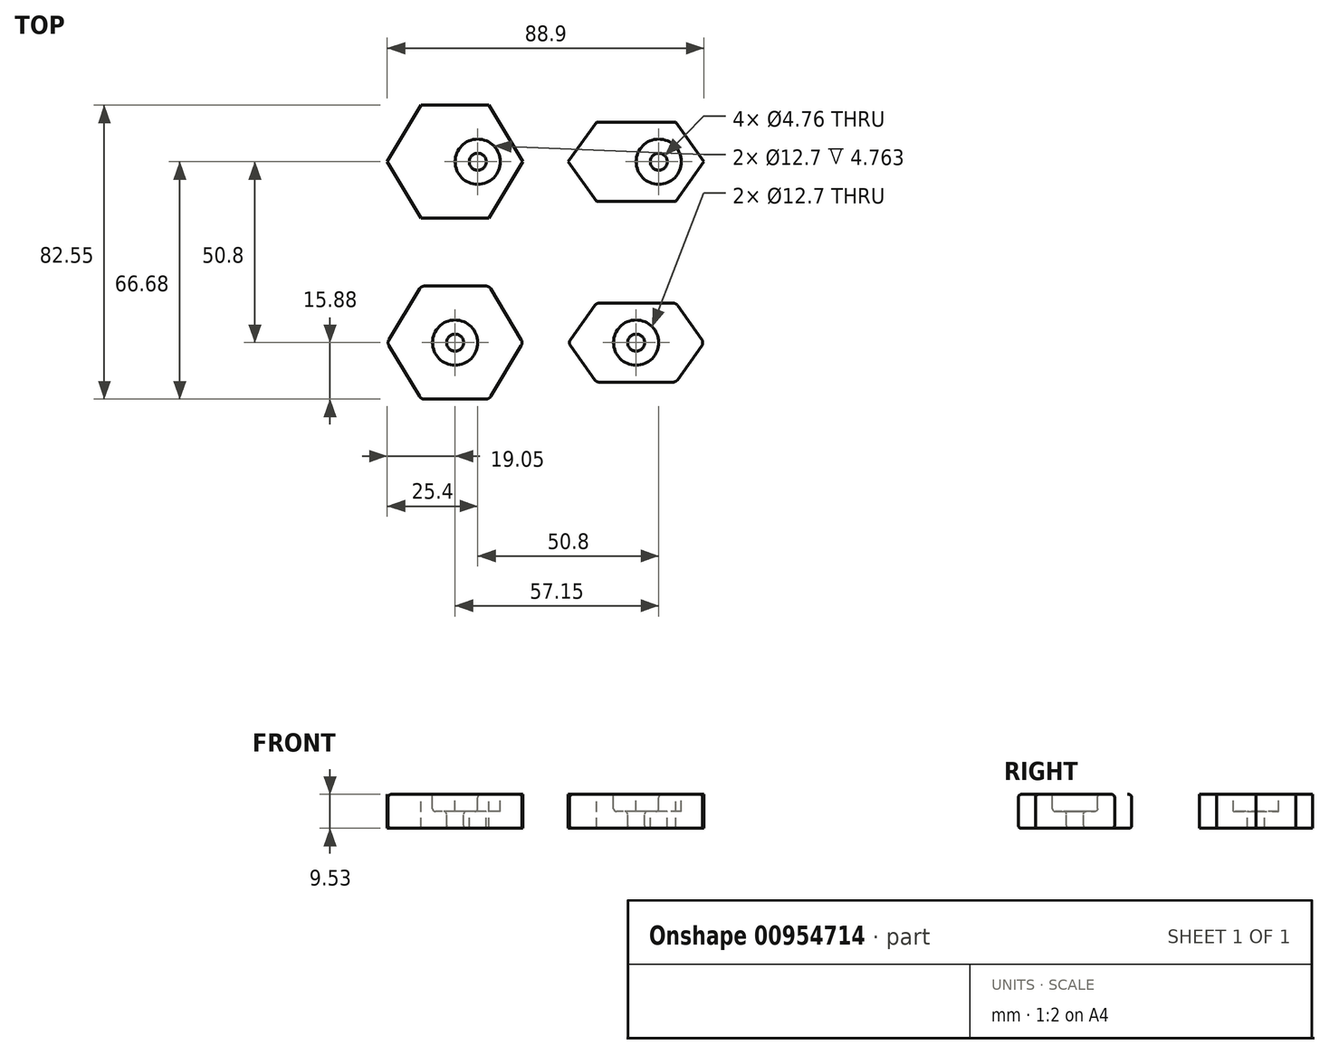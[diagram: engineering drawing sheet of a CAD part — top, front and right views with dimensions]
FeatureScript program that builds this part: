
annotation { "Feature Type Name" : "Feature", "Feature Type Description" : "" }
export const myFeature = defineFeature(function(context is Context, id is Id, definition is map)
    precondition{}
    {
        {
            var Q0;
            Q0=qCreatedBy(makeId("Top.planeOp"),FACE);
            var sketch = newSketch(context, id + "F0", { "sketchPlane" : qUnion([Q0])});
            skArc(sketch, "E0", {"start": v(61.09, 11.11) * mm, "mid": v(61.82, 10.94) * mm, "end": v(62.4, 10.44) * mm});
            skLineSegment(sketch, "E1", {"start": v(62.4, 10.44) * mm, "end": v(69.18, 0.93) * mm});
            skArc(sketch, "E2", {"start": v(69.18, 0.93) * mm, "mid": v(69.49, 0) * mm, "end": v(69.18, -0.93) * mm});
            skLineSegment(sketch, "E3", {"start": v(69.18, -0.93) * mm, "end": v(62.4, -10.44) * mm});
            skArc(sketch, "E4", {"start": v(62.4, -10.44) * mm, "mid": v(61.82, -10.94) * mm, "end": v(61.09, -11.11) * mm});
            skLineSegment(sketch, "E5", {"start": v(61.09, -11.11) * mm, "end": v(40.51, -11.11) * mm});
            skArc(sketch, "E6", {"start": v(40.51, -11.11) * mm, "mid": v(39.78, -10.94) * mm, "end": v(39.2, -10.44) * mm});
            skLineSegment(sketch, "E7", {"start": v(39.2, -10.44) * mm, "end": v(32.42, -0.93) * mm});
            skArc(sketch, "E8", {"start": v(32.42, -0.93) * mm, "mid": v(32.11, 0) * mm, "end": v(32.42, 0.93) * mm});
            skLineSegment(sketch, "E9", {"start": v(32.42, 0.93) * mm, "end": v(39.2, 10.44) * mm});
            skArc(sketch, "E10", {"start": v(39.2, 10.44) * mm, "mid": v(39.78, 10.94) * mm, "end": v(40.51, 11.11) * mm});
            skLineSegment(sketch, "E11", {"start": v(40.51, 11.11) * mm, "end": v(61.09, 11.11) * mm});
            skArc(sketch, "E12", {"start": v(-18.55, -0.83) * mm, "mid": v(-18.79, 0) * mm, "end": v(-18.55, 0.83) * mm});
            skLineSegment(sketch, "E13", {"start": v(-18.55, 0.83) * mm, "end": v(-10, 15.1) * mm});
            skArc(sketch, "E14", {"start": v(-10, 15.1) * mm, "mid": v(-9.4, 15.67) * mm, "end": v(-8.62, 15.87) * mm});
            skLineSegment(sketch, "E15", {"start": v(-8.62, 15.88) * mm, "end": v(8.62, 15.88) * mm});
            skArc(sketch, "E16", {"start": v(8.62, 15.87) * mm, "mid": v(9.4, 15.67) * mm, "end": v(10, 15.1) * mm});
            skLineSegment(sketch, "E17", {"start": v(10, 15.1) * mm, "end": v(18.55, 0.83) * mm});
            skArc(sketch, "E18", {"start": v(18.55, 0.83) * mm, "mid": v(18.79, 0) * mm, "end": v(18.55, -0.83) * mm});
            skLineSegment(sketch, "E19", {"start": v(18.55, -0.83) * mm, "end": v(10, -15.1) * mm});
            skArc(sketch, "E20", {"start": v(10, -15.1) * mm, "mid": v(9.4, -15.67) * mm, "end": v(8.62, -15.87) * mm});
            skLineSegment(sketch, "E21", {"start": v(8.62, -15.88) * mm, "end": v(-8.62, -15.88) * mm});
            skArc(sketch, "E22", {"start": v(-8.62, -15.87) * mm, "mid": v(-9.4, -15.67) * mm, "end": v(-10, -15.1) * mm});
            skLineSegment(sketch, "E23", {"start": v(-10, -15.1) * mm, "end": v(-18.55, -0.83) * mm});
            skArc(sketch, "E24", {"start": v(3.97, 50.8) * mm, "mid": v(4.67, 49.12) * mm, "end": v(6.35, 48.42) * mm});
            skArc(sketch, "E25", {"start": v(6.35, 48.42) * mm, "mid": v(8.03, 49.12) * mm, "end": v(8.73, 50.8) * mm});
            skArc(sketch, "E26", {"start": v(8.73, 50.8) * mm, "mid": v(8.03, 52.48) * mm, "end": v(6.35, 53.18) * mm});
            skArc(sketch, "E27", {"start": v(6.35, 53.18) * mm, "mid": v(4.67, 52.48) * mm, "end": v(3.97, 50.8) * mm});
            skArc(sketch, "E28", {"start": v(0, 50.8) * mm, "mid": v(1.86, 55.3) * mm, "end": v(6.35, 57.15) * mm});
            skArc(sketch, "E29", {"start": v(6.35, 57.15) * mm, "mid": v(10.84, 55.3) * mm, "end": v(12.7, 50.8) * mm});
            skArc(sketch, "E30", {"start": v(12.7, 50.8) * mm, "mid": v(10.84, 46.3) * mm, "end": v(6.35, 44.45) * mm});
            skArc(sketch, "E31", {"start": v(6.35, 44.45) * mm, "mid": v(1.86, 46.3) * mm, "end": v(0, 50.8) * mm});
            skLineSegment(sketch, "E32", {"start": v(-9.53, 34.93) * mm, "end": v(-19.05, 50.8) * mm});
            skLineSegment(sketch, "E33", {"start": v(-19.05, 50.8) * mm, "end": v(-9.52, 66.68) * mm});
            skLineSegment(sketch, "E34", {"start": v(-9.53, 66.68) * mm, "end": v(9.53, 66.68) * mm});
            skLineSegment(sketch, "E35", {"start": v(9.53, 66.68) * mm, "end": v(19.05, 50.8) * mm});
            skLineSegment(sketch, "E36", {"start": v(19.05, 50.8) * mm, "end": v(9.52, 34.92) * mm});
            skLineSegment(sketch, "E37", {"start": v(9.53, 34.93) * mm, "end": v(-9.53, 34.93) * mm});
            skLineSegment(sketch, "E38", {"start": v(39.69, 39.69) * mm, "end": v(31.75, 50.8) * mm});
            skLineSegment(sketch, "E39", {"start": v(31.75, 50.8) * mm, "end": v(39.69, 61.91) * mm});
            skLineSegment(sketch, "E40", {"start": v(39.69, 61.91) * mm, "end": v(61.91, 61.91) * mm});
            skLineSegment(sketch, "E41", {"start": v(61.91, 61.91) * mm, "end": v(69.85, 50.8) * mm});
            skLineSegment(sketch, "E42", {"start": v(69.85, 50.8) * mm, "end": v(61.91, 39.69) * mm});
            skLineSegment(sketch, "E43", {"start": v(61.91, 39.69) * mm, "end": v(39.69, 39.69) * mm});
            skArc(sketch, "E44", {"start": v(54.77, 50.8) * mm, "mid": v(55.47, 49.12) * mm, "end": v(57.15, 48.42) * mm});
            skArc(sketch, "E45", {"start": v(57.15, 48.42) * mm, "mid": v(58.83, 49.12) * mm, "end": v(59.53, 50.8) * mm});
            skArc(sketch, "E46", {"start": v(59.53, 50.8) * mm, "mid": v(58.83, 52.48) * mm, "end": v(57.15, 53.18) * mm});
            skArc(sketch, "E47", {"start": v(57.15, 53.18) * mm, "mid": v(55.47, 52.48) * mm, "end": v(54.77, 50.8) * mm});
            skArc(sketch, "E48", {"start": v(50.8, 50.8) * mm, "mid": v(52.66, 55.3) * mm, "end": v(57.15, 57.15) * mm});
            skArc(sketch, "E49", {"start": v(57.15, 57.15) * mm, "mid": v(61.64, 55.3) * mm, "end": v(63.5, 50.8) * mm});
            skArc(sketch, "E50", {"start": v(63.5, 50.8) * mm, "mid": v(61.64, 46.3) * mm, "end": v(57.15, 44.45) * mm});
            skArc(sketch, "E51", {"start": v(57.15, 44.45) * mm, "mid": v(52.66, 46.3) * mm, "end": v(50.8, 50.8) * mm});
            skArc(sketch, "E52", {"start": v(-2.38, 0) * mm, "mid": v(-1.68, -1.68) * mm, "end": v(0, -2.38) * mm});
            skArc(sketch, "E53", {"start": v(0, -2.38) * mm, "mid": v(1.68, -1.68) * mm, "end": v(2.38, 0) * mm});
            skArc(sketch, "E54", {"start": v(2.38, 0) * mm, "mid": v(1.68, 1.68) * mm, "end": v(0, 2.38) * mm});
            skArc(sketch, "E55", {"start": v(0, 2.38) * mm, "mid": v(-1.68, 1.68) * mm, "end": v(-2.38, 0) * mm});
            skArc(sketch, "E56", {"start": v(-6.35, 0) * mm, "mid": v(-4.5, 4.5) * mm, "end": v(0, 6.35) * mm});
            skArc(sketch, "E57", {"start": v(0, 6.35) * mm, "mid": v(4.5, 4.5) * mm, "end": v(6.35, 0) * mm});
            skArc(sketch, "E58", {"start": v(6.35, 0) * mm, "mid": v(4.5, -4.5) * mm, "end": v(0, -6.35) * mm});
            skArc(sketch, "E59", {"start": v(0, -6.35) * mm, "mid": v(-4.5, -4.5) * mm, "end": v(-6.35, 0) * mm});
            skArc(sketch, "E60", {"start": v(48.42, 0) * mm, "mid": v(49.12, -1.68) * mm, "end": v(50.8, -2.38) * mm});
            skArc(sketch, "E61", {"start": v(50.8, -2.38) * mm, "mid": v(52.48, -1.68) * mm, "end": v(53.18, 0) * mm});
            skArc(sketch, "E62", {"start": v(53.18, 0) * mm, "mid": v(52.48, 1.68) * mm, "end": v(50.8, 2.38) * mm});
            skArc(sketch, "E63", {"start": v(50.8, 2.38) * mm, "mid": v(49.12, 1.68) * mm, "end": v(48.42, 0) * mm});
            skArc(sketch, "E64", {"start": v(44.45, 0) * mm, "mid": v(46.3, 4.5) * mm, "end": v(50.8, 6.35) * mm});
            skArc(sketch, "E65", {"start": v(50.8, 6.35) * mm, "mid": v(55.3, 4.5) * mm, "end": v(57.15, 0) * mm});
            skArc(sketch, "E66", {"start": v(57.15, 0) * mm, "mid": v(55.3, -4.5) * mm, "end": v(50.8, -6.35) * mm});
            skArc(sketch, "E67", {"start": v(50.8, -6.35) * mm, "mid": v(46.3, -4.5) * mm, "end": v(44.45, 0) * mm});
            skSolve(sketch);
        }
        {
            var Q0;
            Q0 = qSketchRegion(id + "F0", true);
            var Q1;
            Q1=makeQuery(id+"F0.imprint","IMPRINT",FACE,{"disambiguationData":[TD([[makeQuery(id+"F0.imprint","IMPRINT",EDGE,{"derivedFrom":sQuery(id+"F0.wireOp",EDGE,"E52")}),-1.0]])]});
            var Q2;
            Q2=makeQuery(id+"F0.imprint","IMPRINT",FACE,{"disambiguationData":[TD([[makeQuery(id+"F0.imprint","IMPRINT",EDGE,{"derivedFrom":sQuery(id+"F0.wireOp",EDGE,"E24")}),-1.0]])]});
            var Q3;
            Q3=makeQuery(id+"F0.imprint","IMPRINT",FACE,{"disambiguationData":[TD([[makeQuery(id+"F0.imprint","IMPRINT",EDGE,{"derivedFrom":sQuery(id+"F0.wireOp",EDGE,"E44")}),-1.0]])]});
            var Q4;
            Q4=makeQuery(id+"F0.imprint","IMPRINT",FACE,{"disambiguationData":[TD([[makeQuery(id+"F0.imprint","IMPRINT",EDGE,{"derivedFrom":sQuery(id+"F0.wireOp",EDGE,"E60")}),-1.0]])]});
            extrude(context, id + "F1", {"entities" : qUnion([Q0, Q1, Q2, Q3, Q4]), "oppositeDirection" : true, "depth" : 9.52 * mm, "offsetDistance" : 25.4 * mm});
        }
        {
            var Q0;
            Q0=makeQuery(id+"F0.imprint","IMPRINT",FACE,{"disambiguationData":[TD([[makeQuery(id+"F0.imprint","IMPRINT",EDGE,{"derivedFrom":sQuery(id+"F0.wireOp",EDGE,"E52")}),-1.0]])]});
            var Q1;
            Q1=makeQuery(id+"F0.imprint","IMPRINT",FACE,{"disambiguationData":[TD([[makeQuery(id+"F0.imprint","IMPRINT",EDGE,{"derivedFrom":sQuery(id+"F0.wireOp",EDGE,"E60")}),-1.0]])]});
            var Q2;
            Q2=makeQuery(id+"F0.imprint","IMPRINT",FACE,{"disambiguationData":[TD([[makeQuery(id+"F0.imprint","IMPRINT",EDGE,{"derivedFrom":sQuery(id+"F0.wireOp",EDGE,"E44")}),-1.0]])]});
            var Q3;
            Q3=makeQuery(id+"F0.imprint","IMPRINT",FACE,{"disambiguationData":[TD([[makeQuery(id+"F0.imprint","IMPRINT",EDGE,{"derivedFrom":sQuery(id+"F0.wireOp",EDGE,"E24")}),-1.0]])]});
            extrude(context, id + "F2", {"entities" : qUnion([Q0, Q1, Q2, Q3]), "operationType" : NewBodyOperationType.REMOVE, "oppositeDirection" : true, "depth" : 4.76 * mm, "offsetDistance" : 25.4 * mm});
        }
        {
            var Q0;
            Q0=makeQuery(id+"F1.opExtrude","CAP_FACE",FACE,{"disambiguationData":[OSD([sQuery(id+"F0.wireOp",EDGE,"E0"),sQuery(id+"F0.wireOp",EDGE,"E1"),sQuery(id+"F0.wireOp",EDGE,"E2"),sQuery(id+"F0.wireOp",EDGE,"E3"),sQuery(id+"F0.wireOp",EDGE,"E4"),sQuery(id+"F0.wireOp",EDGE,"E5"),sQuery(id+"F0.wireOp",EDGE,"E6"),sQuery(id+"F0.wireOp",EDGE,"E7"),sQuery(id+"F0.wireOp",EDGE,"E8"),sQuery(id+"F0.wireOp",EDGE,"E9"),sQuery(id+"F0.wireOp",EDGE,"E10"),sQuery(id+"F0.wireOp",EDGE,"E11"),sQuery(id+"F0.wireOp",EDGE,"E60"),sQuery(id+"F0.wireOp",EDGE,"E61"),sQuery(id+"F0.wireOp",EDGE,"E62"),sQuery(id+"F0.wireOp",EDGE,"E63")])],"isStart":true});
            var Q1;
            Q1=makeQuery(id+"F1.opExtrude","CAP_FACE",FACE,{"disambiguationData":[OSD([sQuery(id+"F0.wireOp",EDGE,"E0"),sQuery(id+"F0.wireOp",EDGE,"E1"),sQuery(id+"F0.wireOp",EDGE,"E2"),sQuery(id+"F0.wireOp",EDGE,"E3"),sQuery(id+"F0.wireOp",EDGE,"E4"),sQuery(id+"F0.wireOp",EDGE,"E5"),sQuery(id+"F0.wireOp",EDGE,"E6"),sQuery(id+"F0.wireOp",EDGE,"E7"),sQuery(id+"F0.wireOp",EDGE,"E8"),sQuery(id+"F0.wireOp",EDGE,"E9"),sQuery(id+"F0.wireOp",EDGE,"E10"),sQuery(id+"F0.wireOp",EDGE,"E11"),sQuery(id+"F0.wireOp",EDGE,"E60"),sQuery(id+"F0.wireOp",EDGE,"E61"),sQuery(id+"F0.wireOp",EDGE,"E62"),sQuery(id+"F0.wireOp",EDGE,"E63")])],"isStart":false});
            var Q2;
            Q2=makeQuery(id+"F2.boolean.opBoolean","COPY",FACE,{"derivedFrom":makeQuery(id+"F2.opExtrude","CAP_FACE",FACE,{"disambiguationData":[OSD([sQuery(id+"F0.wireOp",EDGE,"E60"),sQuery(id+"F0.wireOp",EDGE,"E61"),sQuery(id+"F0.wireOp",EDGE,"E62"),sQuery(id+"F0.wireOp",EDGE,"E63"),sQuery(id+"F0.wireOp",EDGE,"E64"),sQuery(id+"F0.wireOp",EDGE,"E65"),sQuery(id+"F0.wireOp",EDGE,"E66"),sQuery(id+"F0.wireOp",EDGE,"E67")])],"isStart":false})});
            var Q3;
            Q3=makeQuery(id+"F1.opExtrude","CAP_FACE",FACE,{"disambiguationData":[OSD([sQuery(id+"F0.wireOp",EDGE,"E12"),sQuery(id+"F0.wireOp",EDGE,"E13"),sQuery(id+"F0.wireOp",EDGE,"E14"),sQuery(id+"F0.wireOp",EDGE,"E15"),sQuery(id+"F0.wireOp",EDGE,"E16"),sQuery(id+"F0.wireOp",EDGE,"E17"),sQuery(id+"F0.wireOp",EDGE,"E18"),sQuery(id+"F0.wireOp",EDGE,"E19"),sQuery(id+"F0.wireOp",EDGE,"E20"),sQuery(id+"F0.wireOp",EDGE,"E21"),sQuery(id+"F0.wireOp",EDGE,"E22"),sQuery(id+"F0.wireOp",EDGE,"E23"),sQuery(id+"F0.wireOp",EDGE,"E52"),sQuery(id+"F0.wireOp",EDGE,"E53"),sQuery(id+"F0.wireOp",EDGE,"E54"),sQuery(id+"F0.wireOp",EDGE,"E55")])],"isStart":true});
            var Q4;
            Q4=makeQuery(id+"F2.boolean.opBoolean","COPY",FACE,{"derivedFrom":makeQuery(id+"F2.opExtrude","CAP_FACE",FACE,{"disambiguationData":[OSD([sQuery(id+"F0.wireOp",EDGE,"E52"),sQuery(id+"F0.wireOp",EDGE,"E53"),sQuery(id+"F0.wireOp",EDGE,"E54"),sQuery(id+"F0.wireOp",EDGE,"E55"),sQuery(id+"F0.wireOp",EDGE,"E56"),sQuery(id+"F0.wireOp",EDGE,"E57"),sQuery(id+"F0.wireOp",EDGE,"E58"),sQuery(id+"F0.wireOp",EDGE,"E59")])],"isStart":false})});
            var Q5;
            Q5=makeQuery(id+"F1.opExtrude","CAP_FACE",FACE,{"disambiguationData":[OSD([sQuery(id+"F0.wireOp",EDGE,"E12"),sQuery(id+"F0.wireOp",EDGE,"E13"),sQuery(id+"F0.wireOp",EDGE,"E14"),sQuery(id+"F0.wireOp",EDGE,"E15"),sQuery(id+"F0.wireOp",EDGE,"E16"),sQuery(id+"F0.wireOp",EDGE,"E17"),sQuery(id+"F0.wireOp",EDGE,"E18"),sQuery(id+"F0.wireOp",EDGE,"E19"),sQuery(id+"F0.wireOp",EDGE,"E20"),sQuery(id+"F0.wireOp",EDGE,"E21"),sQuery(id+"F0.wireOp",EDGE,"E22"),sQuery(id+"F0.wireOp",EDGE,"E23"),sQuery(id+"F0.wireOp",EDGE,"E52"),sQuery(id+"F0.wireOp",EDGE,"E53"),sQuery(id+"F0.wireOp",EDGE,"E54"),sQuery(id+"F0.wireOp",EDGE,"E55")])],"isStart":false});
            fillet(context, id + "F3", {"entities" : qUnion([Q0, Q1, Q2, Q3, Q4, Q5]), "radius" : 0.8 * mm, "tangentPropagation" : true, "allowEdgeOverflow" : false});
        }
    });
